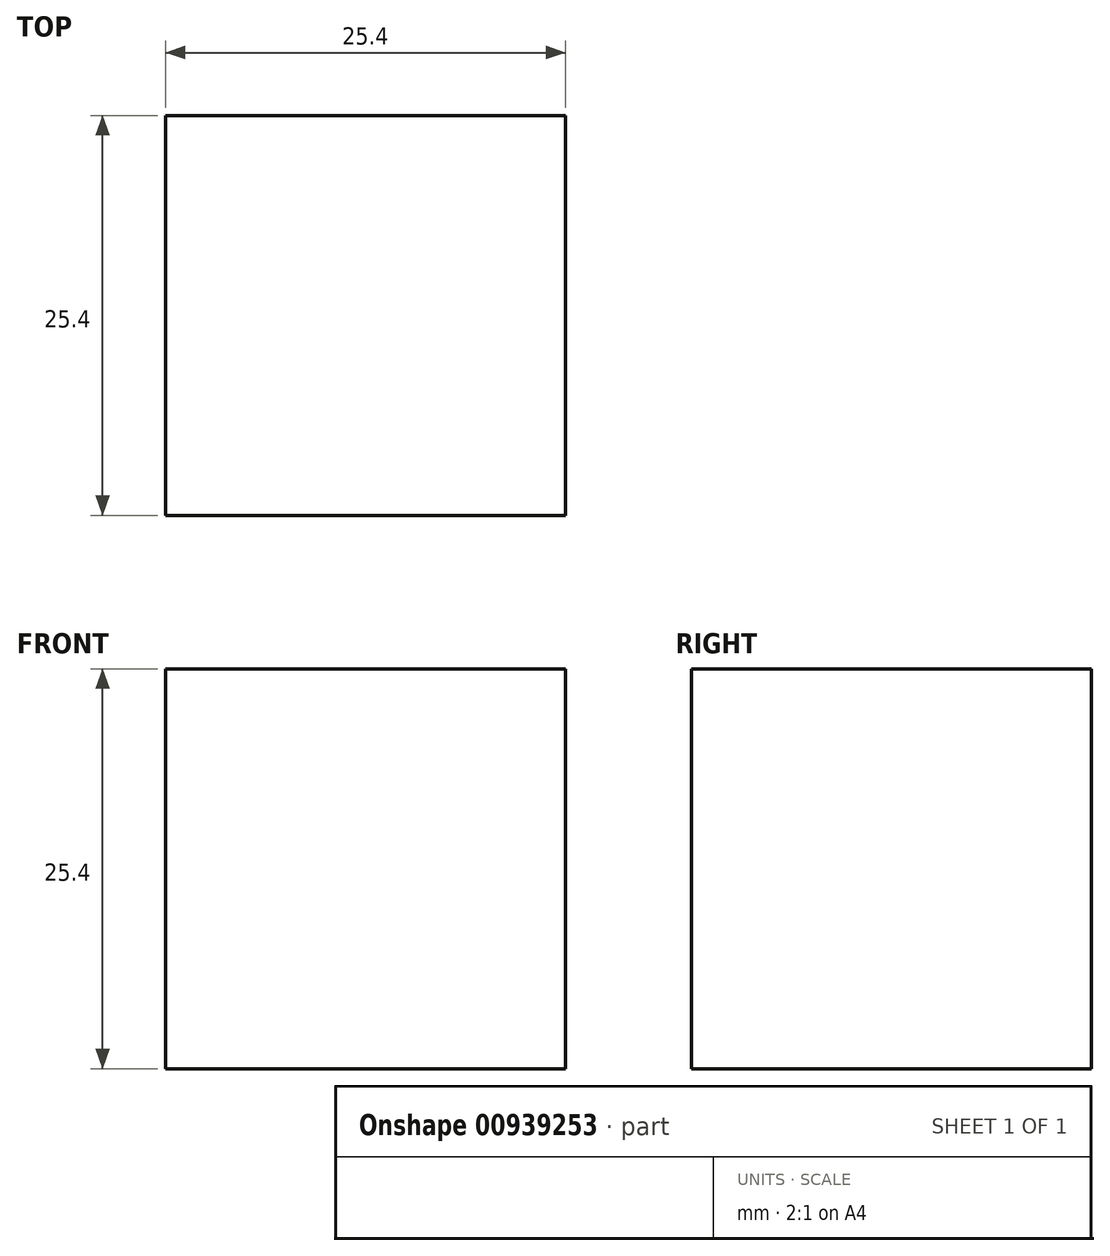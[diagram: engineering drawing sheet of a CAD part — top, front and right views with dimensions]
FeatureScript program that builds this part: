
annotation { "Feature Type Name" : "Feature", "Feature Type Description" : "" }
export const myFeature = defineFeature(function(context is Context, id is Id, definition is map)
    precondition{}
    {
        {
            var Q0;
            Q0=qCreatedBy(makeId("Top.planeOp"),FACE);
            var sketch = newSketch(context, id + "F0", { "sketchPlane" : qUnion([Q0])});
            skLineSegment(sketch, "E0.bottom", {"start": v(-27.55, 26.33) * mm, "end": v(-52.95, 26.33) * mm});
            skLineSegment(sketch, "E0.top", {"start": v(-27.55, 51.73) * mm, "end": v(-52.95, 51.73) * mm});
            skLineSegment(sketch, "E0.left", {"start": v(-27.55, 26.33) * mm, "end": v(-27.55, 51.73) * mm});
            skLineSegment(sketch, "E0.right", {"start": v(-52.95, 26.33) * mm, "end": v(-52.95, 51.73) * mm});
            skSolve(sketch);
        }
        {
            var Q0;
            Q0=makeQuery(id+"F0.imprint","IMPRINT",FACE,{"disambiguationData":[TD([[makeQuery(id+"F0.imprint","IMPRINT",EDGE,{"derivedFrom":sQuery(id+"F0.wireOp",EDGE,"E0.bottom")}),-1.0]])]});
            extrude(context, id + "F1", {"entities" : qUnion([Q0]), "depth" : 25.4 * mm, "offsetDistance" : 25.4 * mm});
        }
    });
